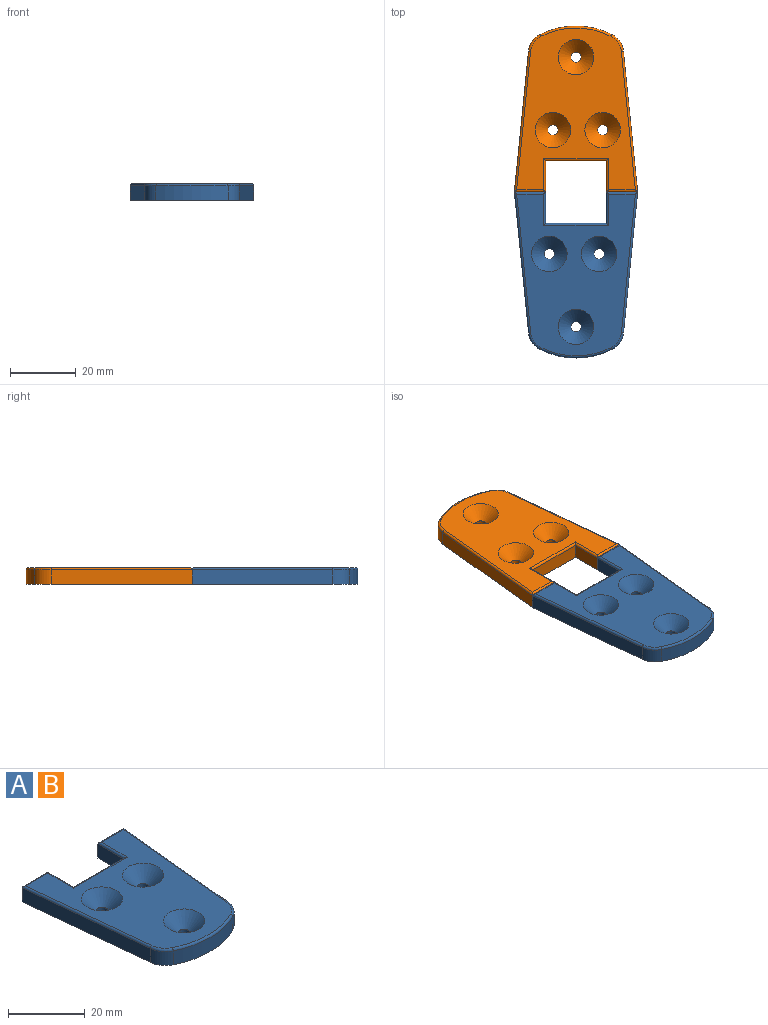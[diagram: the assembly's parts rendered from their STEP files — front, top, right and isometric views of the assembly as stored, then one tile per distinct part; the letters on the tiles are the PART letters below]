
ASSEMBLY  parts=2 mates=1
PART A: 28 faces, bbox 37.6x52.7x5.1 mm
  f0: cylinder r=6.35mm len=5.04mm, axis (0,0,-1), area 28.4mm2, adj f1,f12,f14,f23
  f1: cylinder r=24.62mm len=22mm, axis (0,0,-1), area 101.4mm2, adj f0,f2,f14,f21
  f2: cylinder r=6.35mm len=5.05mm, axis (0,0,-1), area 28.5mm2, adj f1,f3,f14,f19
  f3: plane 43x4.45mm, normal (1,-0.1,0), area 192.1mm2, adj f2,f4,f14,f18
  f4: plane 9.53x4.45mm, normal (0,1,0), area 42.3mm2, adj f3,f5,f14,f20
  f5: plane 9.53x4.45mm, normal (-1,0,0), area 42.3mm2, adj f4,f6,f14,f22
  f6: plane 18.54x4.45mm, normal (0,1,0), area 82.4mm2, adj f5,f7,f14,f24
  f7: plane 9.53x4.45mm, normal (1,0,0), area 42.3mm2, adj f6,f8,f14,f26
  f8: plane 9.53x4.45mm, normal (0,1,0), area 42.3mm2, adj f7,f12,f14,f27
  f9: cylinder r=1.59mm len=3.19mm, axis (0,0,-1), area 12.7mm2, adj f14,f15
  f10: cylinder r=1.59mm len=3.19mm, axis (0,0,-1), area 12.7mm2, adj f14,f16
  f11: cylinder r=1.59mm len=3.19mm, axis (0,0,-1), area 12.7mm2, adj f14,f17
  f12: plane 43x4.45mm, normal (-0.99,-0.1,0), area 192.1mm2, adj f0,f8,f14,f25
  f13: plane 49.37x36.19mm, normal (0,0,1), area 1040.6mm2, adj f15,f16,f17,f18,f19,f20,f21,f22
  f14: plane 50.64x37.59mm, normal (0,0,-1), area 1403.9mm2, adj f0,f1,f2,f3,f4,f5,f6,f7
  f15: cone r=1.59mm half-angle=45deg, axis (0,0,1), area 118.5mm2, adj f9,f13
  f16: cone r=1.59mm half-angle=45deg, axis (0,0,1), area 118.5mm2, adj f10,f13
  f17: cone r=1.59mm half-angle=45deg, axis (0,0,1), area 118.5mm2, adj f11,f13
  f18: cylinder r=0.64mm len=43.06mm, axis (-0.1,-1,0), area 42.8mm2, adj f3,f13,f19,f20
  f19: torus R=5.71mm, axis (0,0,1), area 6.2mm2, adj f2,f13,f18,f21
  f20: cylinder r=0.64mm len=9.53mm, axis (1,0,0), area 9mm2, adj f4,f13,f18,f22
  f21: torus R=23.99mm, axis (0,0,1), area 22.5mm2, adj f1,f13,f19,f23
  f22: cylinder r=0.64mm len=10.16mm, axis (0,1,0), area 9.5mm2, adj f5,f13,f20,f24
  f23: torus R=5.71mm, axis (0,0,1), area 6.1mm2, adj f0,f13,f21,f25
  f24: cylinder r=0.64mm len=19.81mm, axis (1,0,0), area 19mm2, adj f6,f13,f22,f26
  f25: cylinder r=0.64mm len=43.06mm, axis (-0.1,0.99,0), area 42.8mm2, adj f12,f13,f23,f27
  f26: cylinder r=0.64mm len=10.16mm, axis (0,-1,0), area 9.5mm2, adj f7,f13,f24,f27
  f27: cylinder r=0.64mm len=9.53mm, axis (1,0,0), area 9mm2, adj f8,f13,f25,f26
PART B: same geometry as A
PLACE A rot(axis=(0,0,1),0deg) t=(18.57,-61.26,0.04)mm
PLACE B rot(axis=(0,0,-1),180deg) t=(56.15,40.34,0.04)mm fixed
MATE planar B.f4 <-> A.f8  axis (0,-1,0) through (23.33,-10.46,2.26)mm
